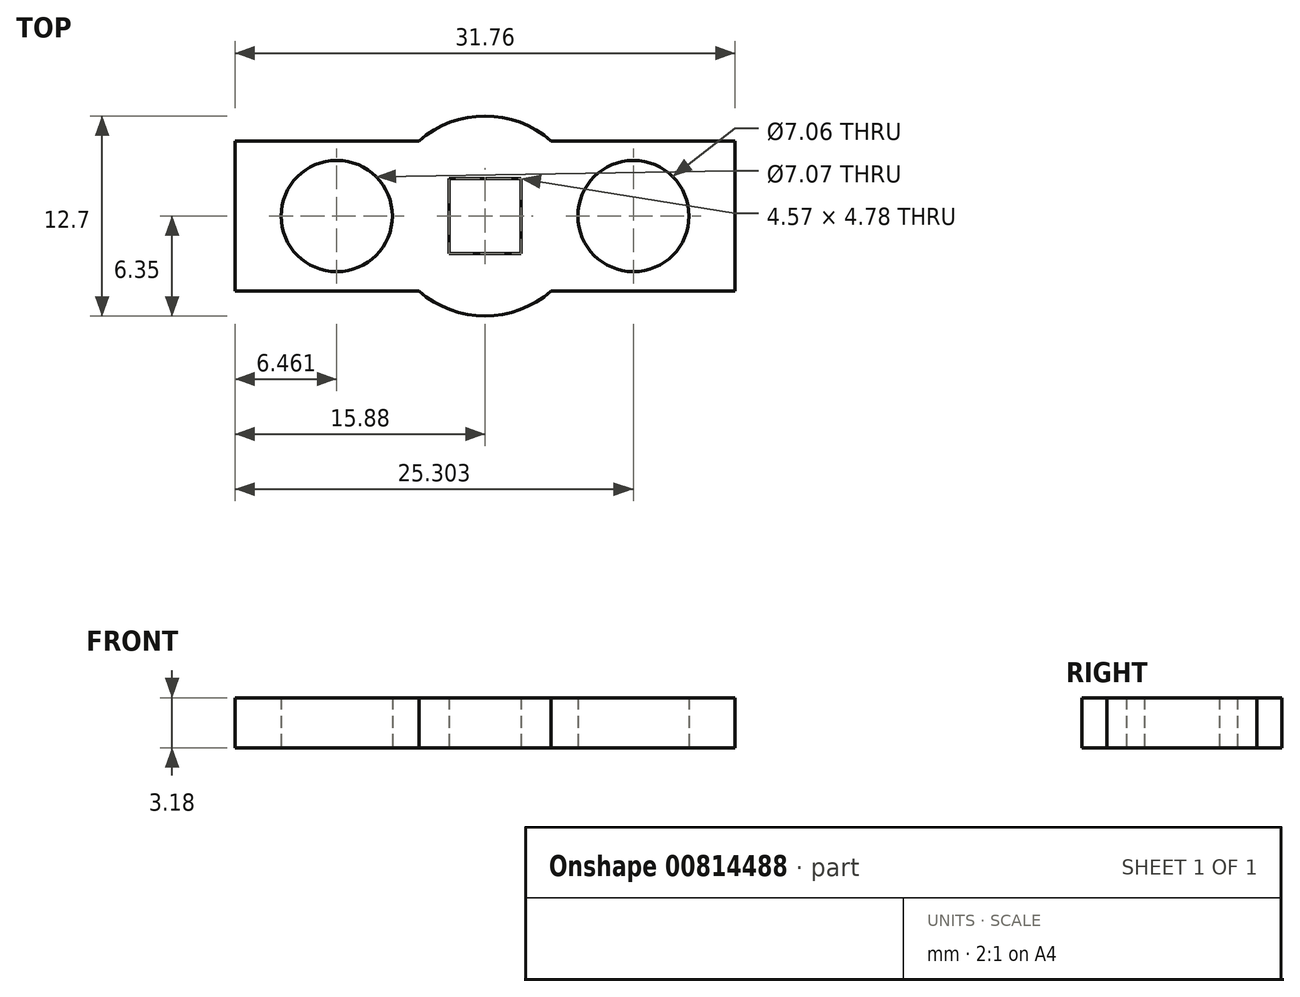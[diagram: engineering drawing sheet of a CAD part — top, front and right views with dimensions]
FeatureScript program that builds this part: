
annotation { "Feature Type Name" : "Feature", "Feature Type Description" : "" }
export const myFeature = defineFeature(function(context is Context, id is Id, definition is map)
    precondition{}
    {
        {
            var Q0;
            Q0=qCreatedBy(makeId("Top.planeOp"),FACE);
            var sketch = newSketch(context, id + "F0", { "sketchPlane" : qUnion([Q0])});
            skCircle(sketch, "E0", {"center": v(0, 0) * mm, "radius": 6.35 * mm});
            skLineSegment(sketch, "E1.bottom", {"start": v(-3.17, -4.76) * mm, "end": v(-15.88, -4.76) * mm});
            skLineSegment(sketch, "E1.top", {"start": v(-3.17, 4.76) * mm, "end": v(-15.88, 4.76) * mm});
            skLineSegment(sketch, "E1.left", {"start": v(-3.17, -4.76) * mm, "end": v(-3.17, 4.76) * mm});
            skLineSegment(sketch, "E1.right", {"start": v(-15.88, -4.76) * mm, "end": v(-15.88, 4.76) * mm});
            skPoint(sketch, "E1.middle", {"position": v(-9.52, 0) * mm});
            skLineSegment(sketch, "E2.bottom", {"start": v(15.88, -4.76) * mm, "end": v(3.17, -4.76) * mm});
            skLineSegment(sketch, "E2.top", {"start": v(15.88, 4.76) * mm, "end": v(3.18, 4.76) * mm});
            skLineSegment(sketch, "E2.left", {"start": v(15.88, -4.76) * mm, "end": v(15.88, 4.76) * mm});
            skLineSegment(sketch, "E2.right", {"start": v(3.17, -4.76) * mm, "end": v(3.17, 4.76) * mm});
            skPoint(sketch, "E2.middle", {"position": v(9.52, 0) * mm});
            skSolve(sketch);
        }
        {
            var Q0;
            Q0=qCreatedBy(makeId("Top.planeOp"),FACE);
            var sketch = newSketch(context, id + "F1", { "sketchPlane" : qUnion([Q0])});
            skLineSegment(sketch, "E3.bottom", {"start": v(2.29, -2.39) * mm, "end": v(-2.29, -2.39) * mm});
            skLineSegment(sketch, "E3.top", {"start": v(2.29, 2.39) * mm, "end": v(-2.29, 2.39) * mm});
            skLineSegment(sketch, "E3.left", {"start": v(2.29, -2.39) * mm, "end": v(2.29, 2.39) * mm});
            skLineSegment(sketch, "E3.right", {"start": v(-2.29, -2.39) * mm, "end": v(-2.29, 2.39) * mm});
            skPoint(sketch, "E3.middle", {"position": v(0, 0) * mm});
            skCircle(sketch, "E4", {"center": v(9.42, 0) * mm, "radius": 3.53 * mm});
            skCircle(sketch, "E5", {"center": v(-9.42, 0) * mm, "radius": 3.53 * mm});
            skSolve(sketch);
        }
        {
            var Q0;
            Q0 = qSketchRegion(id + "F0", true);
            extrude(context, id + "F2", {"entities" : qUnion([Q0]), "endBound" : BoundingType.SYMMETRIC, "depth" : 3.17 * mm, "offsetDistance" : 25.4 * mm});
        }
        {
            var Q0;
            Q0 = qSketchRegion(id + "F1", true);
            extrude(context, id + "F3", {"entities" : qUnion([Q0]), "operationType" : NewBodyOperationType.REMOVE, "endBound" : BoundingType.SYMMETRIC, "depth" : 3.17 * mm, "offsetDistance" : 25.4 * mm});
        }
    });
